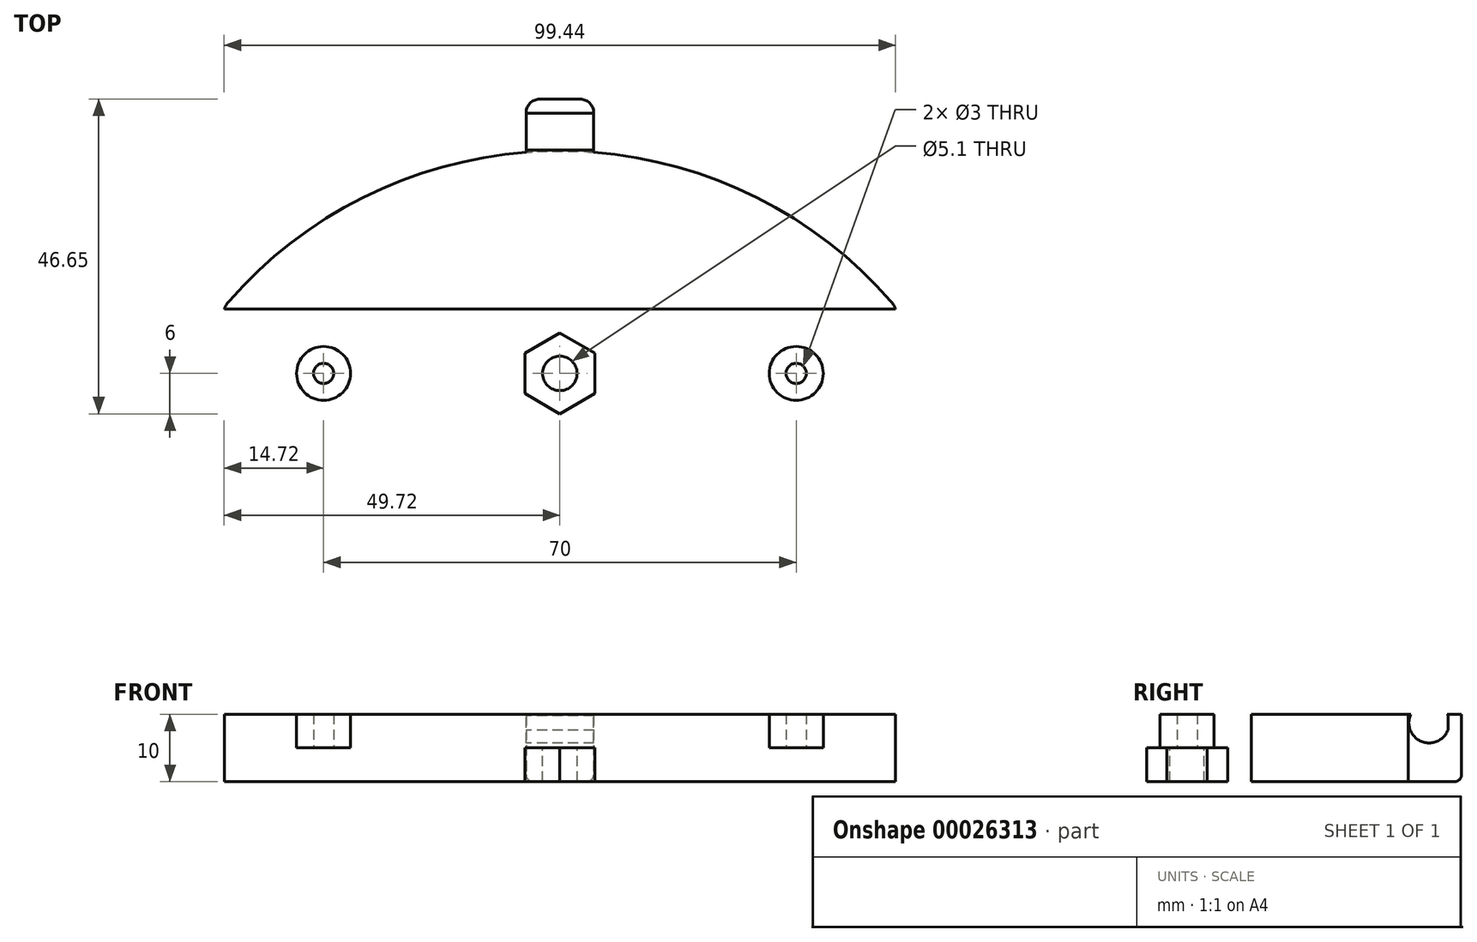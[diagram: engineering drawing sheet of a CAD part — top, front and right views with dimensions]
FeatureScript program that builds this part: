
annotation { "Feature Type Name" : "Feature", "Feature Type Description" : "" }
export const myFeature = defineFeature(function(context is Context, id is Id, definition is map)
    precondition{}
    {
        {
            var Q0;
            Q0=qCreatedBy(makeId("Top.planeOp"),FACE);
            var sketch = newSketch(context, id + "F0", { "sketchPlane" : qUnion([Q0])});
            skLineSegment(sketch, "E0.rect.bottom", {"start": v(-50, 9.54) * mm, "end": v(50, 9.54) * mm});
            skLineSegment(sketch, "E0.rect.top", {"start": v(-46, -9.54) * mm, "end": v(46, -9.54) * mm});
            skLineSegment(sketch, "E0.rect.left", {"start": v(-50, 8.06) * mm, "end": v(-50, -5.54) * mm});
            skLineSegment(sketch, "E0.rect.right", {"start": v(50, 8.06) * mm, "end": v(50, -5.54) * mm});
            skPoint(sketch, "E0.rect.middle", {"position": v(0, 0) * mm});
            skArc(sketch, "E1", {"start": v(49.01, 10.7) * mm, "mid": v(0, 32.95) * mm, "end": v(-49.01, 10.7) * mm});
            skPoint(sketch, "E2.visualSharp", {"position": v(-50, -9.54) * mm});
            skArc(sketch, "E2.filletArc", {"start": v(-50, -5.54) * mm, "mid": v(-48.83, -8.37) * mm, "end": v(-46, -9.54) * mm});
            skPoint(sketch, "E3.visualSharp", {"position": v(50, -9.54) * mm});
            skArc(sketch, "E3.filletArc", {"start": v(46, -9.54) * mm, "mid": v(48.83, -8.37) * mm, "end": v(50, -5.54) * mm});
            skPoint(sketch, "E4.visualSharp", {"position": v(-50, 9.54) * mm});
            skArc(sketch, "E4.filletArc", {"start": v(-49.01, 10.7) * mm, "mid": v(-49.74, 9.47) * mm, "end": v(-50, 8.06) * mm});
            skPoint(sketch, "E5.visualSharp", {"position": v(50, 9.54) * mm});
            skArc(sketch, "E5.filletArc", {"start": v(50, 8.06) * mm, "mid": v(49.74, 9.47) * mm, "end": v(49.01, 10.7) * mm});
            skCircle(sketch, "E6.cCircle", {"center": v(0, 0) * mm, "radius": 5.2 * mm, "construction": true});
            skLineSegment(sketch, "E6.0", {"start": v(5.2, 3) * mm, "end": v(5.2, -3) * mm});
            skLineSegment(sketch, "E6.1", {"start": v(5.2, -3) * mm, "end": v(0, -6) * mm});
            skLineSegment(sketch, "E6.2", {"start": v(0, -6) * mm, "end": v(-5.2, -3) * mm});
            skLineSegment(sketch, "E6.3", {"start": v(-5.2, -3) * mm, "end": v(-5.2, 3) * mm});
            skLineSegment(sketch, "E6.4", {"start": v(-5.2, 3) * mm, "end": v(0, 6) * mm});
            skLineSegment(sketch, "E6.5", {"start": v(0, 6) * mm, "end": v(5.2, 3) * mm});
            skPoint(sketch, "E6.0.midPoint", {"position": v(5.2, 0) * mm});
            skCircle(sketch, "E7", {"center": v(-35, 0) * mm, "radius": 1.5 * mm});
            skCircle(sketch, "E8", {"center": v(35, 0) * mm, "radius": 1.5 * mm});
            skCircle(sketch, "E9", {"center": v(35, 0) * mm, "radius": 4 * mm});
            skCircle(sketch, "E10", {"center": v(-35, 0) * mm, "radius": 4 * mm});
            skCircle(sketch, "E11", {"center": v(0, 0) * mm, "radius": 2.55 * mm});
            skLineSegment(sketch, "E12", {"start": v(0, 0) * mm, "end": v(0, 50.77) * mm, "construction": true});
            skLineSegment(sketch, "E13", {"start": v(5, 38.65) * mm, "end": v(5, 9.54) * mm});
            skLineSegment(sketch, "E14", {"start": v(3, 40.65) * mm, "end": v(-3, 40.65) * mm});
            skLineSegment(sketch, "E15", {"start": v(-5, 38.65) * mm, "end": v(-5, 9.54) * mm});
            skPoint(sketch, "E16.visualSharp", {"position": v(-5, 40.65) * mm});
            skArc(sketch, "E16.filletArc", {"start": v(-3, 40.65) * mm, "mid": v(-4.41, 40.06) * mm, "end": v(-5, 38.65) * mm});
            skPoint(sketch, "E17.visualSharp", {"position": v(5, 40.65) * mm});
            skArc(sketch, "E17.filletArc", {"start": v(5, 38.65) * mm, "mid": v(4.41, 40.06) * mm, "end": v(3, 40.65) * mm});
            skSolve(sketch);
        }
        {
            var Q0;
            Q0=makeQuery(id+"F0.imprint","IMPRINT",FACE,{"disambiguationData":[TD([[makeQuery(id+"F0.imprint","IMPRINT",EDGE,{"derivedFrom":sQuery(id+"F0.wireOp",EDGE,"E0.rect.top")}),1.0]])]});
            var Q1;
            {var subQ3=sQuery(id+"F0.wireOp",EDGE,"E1");Q1=makeQuery(id+"F0.imprint","IMPRINT",FACE,{"disambiguationData":[TD([[makeQuery(id+"F0.imprint","IMPRINT",EDGE,{"derivedFrom":subQ3}),1.0]])]});}
            var Q2;
            Q2=makeQuery(id+"F0.imprint","IMPRINT",FACE,{"disambiguationData":[TD([[makeQuery(id+"F0.imprint","IMPRINT",EDGE,{"derivedFrom":sQuery(id+"F0.wireOp",EDGE,"E7")}),-1.0]])]});
            var Q3;
            Q3=makeQuery(id+"F0.imprint","IMPRINT",FACE,{"disambiguationData":[TD([[makeQuery(id+"F0.imprint","IMPRINT",EDGE,{"derivedFrom":sQuery(id+"F0.wireOp",EDGE,"E8")}),-1.0]])]});
            var Q4;
            Q4=makeQuery(id+"F0.imprint","IMPRINT",FACE,{"disambiguationData":[TD([[makeQuery(id+"F0.imprint","IMPRINT",EDGE,{"derivedFrom":sQuery(id+"F0.wireOp",EDGE,"E14")}),1.0]])]});
            extrude(context, id + "F1", {"entities" : qUnion([Q0, Q1, Q2, Q3, Q4]), "depth" : 5 * mm});
        }
        {
            var Q0;
            {var subQ3=sQuery(id+"F0.wireOp",EDGE,"E1");Q0=makeQuery(id+"F0.imprint","IMPRINT",FACE,{"disambiguationData":[TD([[makeQuery(id+"F0.imprint","IMPRINT",EDGE,{"derivedFrom":subQ3}),1.0]])]});}
            var Q1;
            Q1=makeQuery(id+"F0.imprint","IMPRINT",FACE,{"disambiguationData":[TD([[makeQuery(id+"F0.imprint","IMPRINT",EDGE,{"derivedFrom":sQuery(id+"F0.wireOp",EDGE,"E0.rect.top")}),1.0]])]});
            var Q2;
            Q2=makeQuery(id+"F0.imprint","IMPRINT",FACE,{"disambiguationData":[TD([[makeQuery(id+"F0.imprint","IMPRINT",EDGE,{"derivedFrom":sQuery(id+"F0.wireOp",EDGE,"E6.0")}),-1.0]])]});
            var Q3;
            Q3=makeQuery(id+"F0.imprint","IMPRINT",FACE,{"disambiguationData":[TD([[makeQuery(id+"F0.imprint","IMPRINT",EDGE,{"derivedFrom":sQuery(id+"F0.wireOp",EDGE,"E14")}),1.0]])]});
            extrude(context, id + "F2", {"entities" : qUnion([Q0, Q1, Q2, Q3]), "operationType" : NewBodyOperationType.ADD, "oppositeDirection" : true, "depth" : 5 * mm});
        }
        {
            var Q0;
            Q0=makeQuery(id+"F2.opExtrude","CAP_EDGE",EDGE,{"disambiguationData":[OSD([sQuery(id+"F0.wireOp",EDGE,"E0.rect.left")])],"isStart":false});
            var Q1;
            Q1=makeQuery(id+"F2.opExtrude","CAP_EDGE",EDGE,{"disambiguationData":[OSD([sQuery(id+"F0.wireOp",EDGE,"E2.filletArc")])],"isStart":false});
            var Q2;
            Q2=makeQuery(id+"F2.opExtrude","CAP_EDGE",EDGE,{"disambiguationData":[OSD([sQuery(id+"F0.wireOp",EDGE,"E0.rect.top")])],"isStart":false});
            var Q3;
            Q3=makeQuery(id+"F2.opExtrude","CAP_EDGE",EDGE,{"disambiguationData":[OSD([sQuery(id+"F0.wireOp",EDGE,"E3.filletArc")])],"isStart":false});
            var Q4;
            Q4=makeQuery(id+"F2.opExtrude","CAP_EDGE",EDGE,{"disambiguationData":[OSD([sQuery(id+"F0.wireOp",EDGE,"E0.rect.right")])],"isStart":false});
            var Q5;
            Q5=makeQuery(id+"F2.opExtrude","CAP_EDGE",EDGE,{"disambiguationData":[OSD([sQuery(id+"F0.wireOp",EDGE,"E15")])],"isStart":false});
            fillet(context, id + "F3", {"entities" : qUnion([Q0, Q1, Q2, Q3, Q4, Q5]), "radius" : 1 * mm, "tangentPropagation" : true, "allowEdgeOverflow" : false});
        }
        {
            var Q0;
            {var subQ0=sQuery(id+"F0.wireOp",EDGE,"E15");Q0=makeQuery(id+"F2.boolean.opBoolean","MERGE",FACE,{"derivedFrom":[makeQuery(id+"F1.opExtrude","SWEPT_FACE",FACE,{"disambiguationData":[OSD([subQ0])]}),makeQuery(id+"F2.opExtrude","SWEPT_FACE",FACE,{"disambiguationData":[OSD([subQ0])]})]});}
            var sketch = newSketch(context, id + "F4", { "sketchPlane" : qUnion([Q0])});
            skCircle(sketch, "E18", {"center": v(-35.85, 3.73) * mm, "radius": 3 * mm});
            skSolve(sketch);
        }
        {
            var Q0;
            {var subQ0=sQuery(id+"F0.wireOp",EDGE,"E15");var subQ3=sQuery(id+"F4.wireOp",EDGE,"E18");var subQ6=makeQuery(id+"F1.opExtrude","CAP_EDGE",EDGE,{"disambiguationData":[OSD([subQ0])],"isStart":false});var subQ8=makeQuery(id+"F4.imprint","INTERSECT",VERTEX,{"disambiguationData":[OD(0.0)],"derivedFrom":[subQ6,subQ3]});Q0=makeQuery(id+"F4.imprint","IMPRINT",FACE,{"disambiguationData":[TD([[makeQuery(id+"F4.imprint","IMPRINT",EDGE,{"disambiguationData":[TD([[subQ8,-1.0]])],"derivedFrom":subQ6}),-1.0]])]});}
            var Q1;
            {var subQ0=makeQuery(id+"F1.opExtrude","CAP_EDGE",EDGE,{"disambiguationData":[OSD([sQuery(id+"F0.wireOp",EDGE,"E15")])],"isStart":false});var subQ1=sQuery(id+"F4.wireOp",EDGE,"E18");var subQ3=makeQuery(id+"F4.imprint","INTERSECT",VERTEX,{"disambiguationData":[OD(0.0)],"derivedFrom":[subQ0,subQ1]});Q1=makeQuery(id+"F4.imprint","IMPRINT",FACE,{"disambiguationData":[TD([[makeQuery(id+"F4.imprint","IMPRINT",EDGE,{"disambiguationData":[TD([[subQ3,1.0]])],"derivedFrom":subQ1}),1.0]])]});}
            extrude(context, id + "F5", {"entities" : qUnion([Q0, Q1]), "operationType" : NewBodyOperationType.REMOVE, "oppositeDirection" : true, "depth" : 10 * mm});
        }
    });
